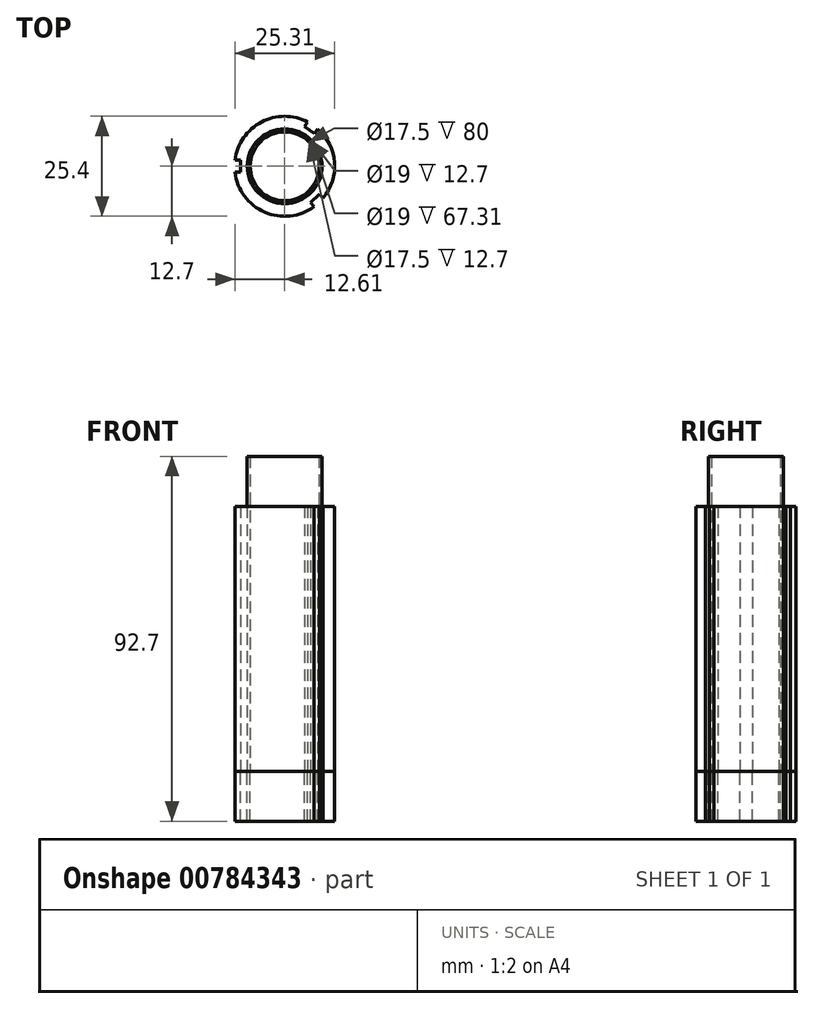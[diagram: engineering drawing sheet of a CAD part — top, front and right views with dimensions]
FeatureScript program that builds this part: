
annotation { "Feature Type Name" : "Feature", "Feature Type Description" : "" }
export const myFeature = defineFeature(function(context is Context, id is Id, definition is map)
    precondition{}
    {
        {
            var Q0;
            Q0=qCreatedBy(makeId("Top.planeOp"),FACE);
            var sketch = newSketch(context, id + "F0", { "sketchPlane" : qUnion([Q0])});
            skCircle(sketch, "E0", {"center": v(0, 0) * mm, "radius": 9.5 * mm});
            skArc(sketch, "E1", {"start": v(9.76, -8.13) * mm, "mid": v(12.66, 0.97) * mm, "end": v(8.42, 9.51) * mm});
            skLineSegment(sketch, "E2", {"start": v(-12.6, 1.6) * mm, "end": v(-11.21, 1.6) * mm});
            skLineSegment(sketch, "E3", {"start": v(-11.21, 1.6) * mm, "end": v(-11.21, -1.5) * mm});
            skLineSegment(sketch, "E4", {"start": v(-11.21, -1.5) * mm, "end": v(-12.61, -1.5) * mm});
            skLineSegment(sketch, "E5", {"start": v(5.86, 11.27) * mm, "end": v(5.07, 10.12) * mm});
            skLineSegment(sketch, "E6", {"start": v(5.07, 10.12) * mm, "end": v(7.62, 8.36) * mm});
            skLineSegment(sketch, "E7", {"start": v(7.62, 8.36) * mm, "end": v(8.42, 9.51) * mm});
            skLineSegment(sketch, "E8", {"start": v(7.5, -10.25) * mm, "end": v(6.54, -9.23) * mm});
            skLineSegment(sketch, "E9", {"start": v(6.54, -9.23) * mm, "end": v(8.8, -7.1) * mm});
            skLineSegment(sketch, "E10", {"start": v(8.8, -7.1) * mm, "end": v(9.76, -8.13) * mm});
            skArc(sketch, "E11.trimOffspring", {"start": v(5.86, 11.27) * mm, "mid": v(-5.89, 11.25) * mm, "end": v(-12.6, 1.6) * mm});
            skArc(sketch, "E12.trimOffspring", {"start": v(-12.61, -1.5) * mm, "mid": v(-5.06, -11.65) * mm, "end": v(7.5, -10.25) * mm});
            skSolve(sketch);
        }
        {
            var Q0;
            Q0=makeQuery(id+"F0.imprint","IMPRINT",FACE,{"disambiguationData":[TD([[makeQuery(id+"F0.imprint","IMPRINT",EDGE,{"derivedFrom":sQuery(id+"F0.wireOp",EDGE,"E0")}),-1.0]])]});
            extrude(context, id + "F1", {"entities" : qUnion([Q0]), "depth" : 67.3 * mm, "offsetDistance" : 25.4 * mm});
        }
        {
            var Q0;
            Q0=qCreatedBy(makeId("Top.planeOp"),FACE);
            var sketch = newSketch(context, id + "F2", { "sketchPlane" : qUnion([Q0])});
            skCircle(sketch, "E13", {"center": v(0, 0) * mm, "radius": 8.75 * mm});
            skCircle(sketch, "E14", {"center": v(0, 0) * mm, "radius": 9.5 * mm});
            skSolve(sketch);
        }
        {
            var Q0;
            Q0=makeQuery(id+"F2.imprint","IMPRINT",FACE,{"disambiguationData":[TD([[makeQuery(id+"F2.imprint","IMPRINT",EDGE,{"derivedFrom":sQuery(id+"F2.wireOp",EDGE,"E13")}),-1.0]])]});
            extrude(context, id + "F3", {"entities" : qUnion([Q0]), "depth" : 80 * mm, "offsetDistance" : 25.4 * mm});
        }
        {
            var Q0;
            Q0=makeQuery(id+"F3.opExtrude","CAP_FACE",FACE,{"disambiguationData":[OSD([sQuery(id+"F2.wireOp",EDGE,"E13"),sQuery(id+"F2.wireOp",EDGE,"E14")])],"isStart":true});
            var Q1;
            Q1=makeQuery(id+"F1.opExtrude","CAP_FACE",FACE,{"disambiguationData":[OSD([sQuery(id+"F0.wireOp",EDGE,"E0"),sQuery(id+"F0.wireOp",EDGE,"E1"),sQuery(id+"F0.wireOp",EDGE,"E2"),sQuery(id+"F0.wireOp",EDGE,"E3"),sQuery(id+"F0.wireOp",EDGE,"E4"),sQuery(id+"F0.wireOp",EDGE,"E5"),sQuery(id+"F0.wireOp",EDGE,"E6"),sQuery(id+"F0.wireOp",EDGE,"E7"),sQuery(id+"F0.wireOp",EDGE,"E8"),sQuery(id+"F0.wireOp",EDGE,"E9"),sQuery(id+"F0.wireOp",EDGE,"E10"),sQuery(id+"F0.wireOp",EDGE,"E11.trimOffspring"),sQuery(id+"F0.wireOp",EDGE,"E12.trimOffspring")])],"isStart":true});
            extrude(context, id + "F4", {"entities" : qUnion([Q0, Q1]), "depth" : 12.7 * mm, "offsetDistance" : 25.4 * mm});
        }
    });
